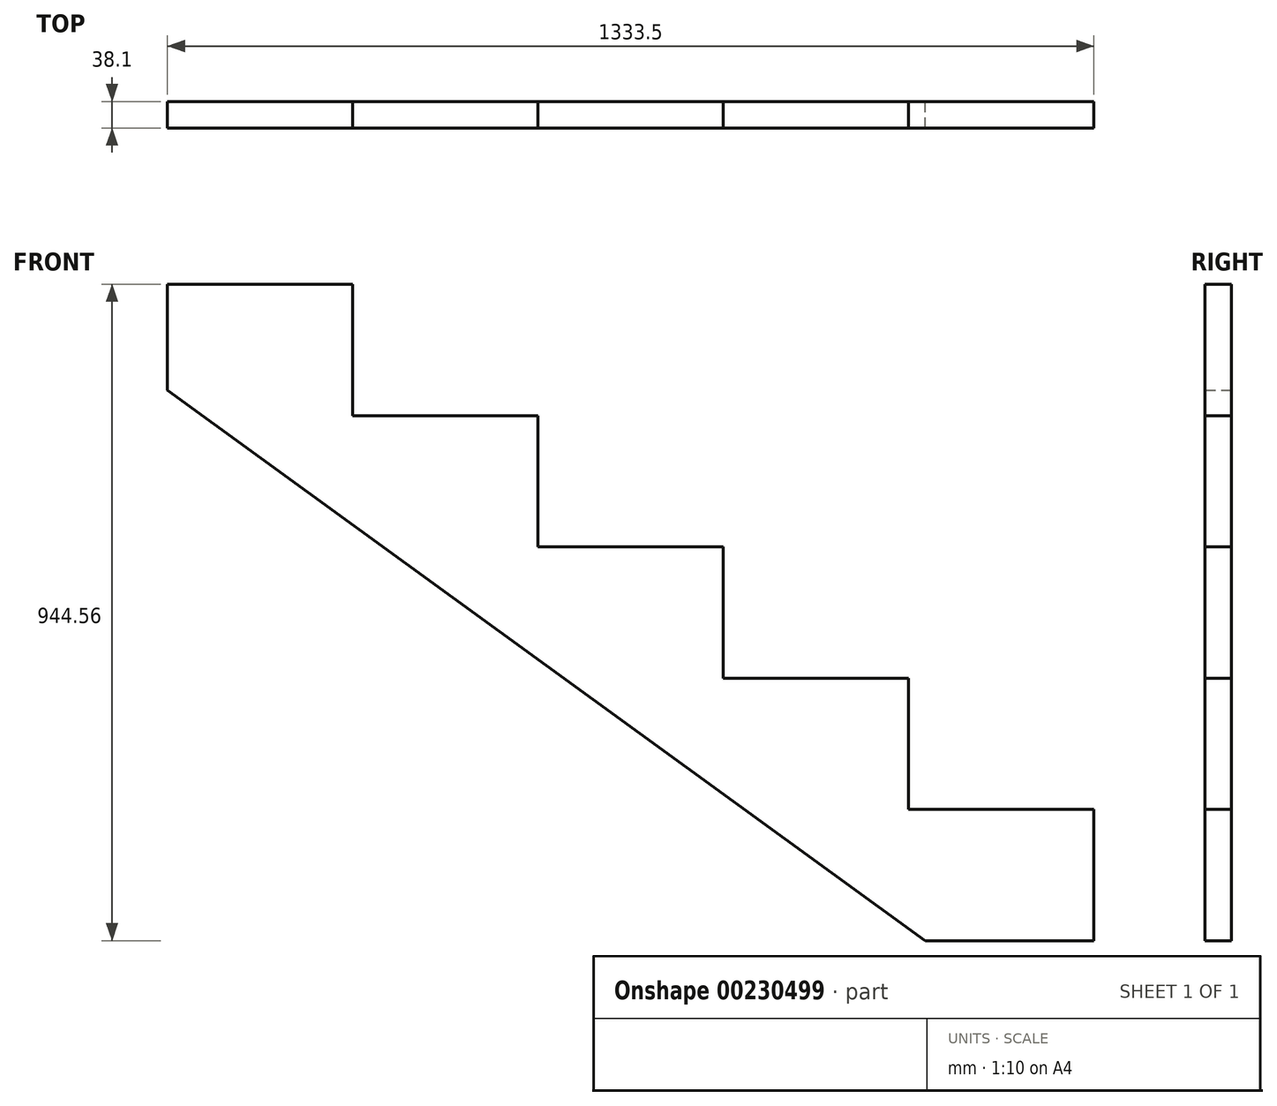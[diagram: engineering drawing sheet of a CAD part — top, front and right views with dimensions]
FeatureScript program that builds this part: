
annotation { "Feature Type Name" : "Feature", "Feature Type Description" : "" }
export const myFeature = defineFeature(function(context is Context, id is Id, definition is map)
    precondition{}
    {
        {
            var Q0;
            Q0=qCreatedBy(makeId("Front.planeOp"),FACE);
            var sketch = newSketch(context, id + "F0", { "sketchPlane" : qUnion([Q0])});
            skLineSegment(sketch, "E0", {"start": v(0, 944.56) * mm, "end": v(0, 792.16) * mm});
            skLineSegment(sketch, "E1", {"start": v(0, 792.16) * mm, "end": v(1090.32, 0) * mm});
            skLineSegment(sketch, "E2", {"start": v(1090.32, 0) * mm, "end": v(1333.5, 0) * mm});
            skLineSegment(sketch, "E3", {"start": v(0, 944.56) * mm, "end": v(266.7, 944.56) * mm});
            skLineSegment(sketch, "E4", {"start": v(1333.5, 0) * mm, "end": v(1333.5, 188.91) * mm});
            skLineSegment(sketch, "E5", {"start": v(1333.5, 188.91) * mm, "end": v(1066.8, 188.91) * mm});
            skLineSegment(sketch, "E6", {"start": v(1066.8, 188.91) * mm, "end": v(1066.8, 377.82) * mm});
            skLineSegment(sketch, "E7", {"start": v(1066.8, 377.83) * mm, "end": v(800.1, 377.83) * mm});
            skLineSegment(sketch, "E8", {"start": v(800.1, 377.83) * mm, "end": v(800.1, 566.74) * mm});
            skLineSegment(sketch, "E9", {"start": v(800.1, 566.74) * mm, "end": v(533.4, 566.74) * mm});
            skLineSegment(sketch, "E10", {"start": v(533.4, 566.74) * mm, "end": v(533.4, 755.65) * mm});
            skLineSegment(sketch, "E11", {"start": v(533.4, 755.65) * mm, "end": v(266.7, 755.65) * mm});
            skLineSegment(sketch, "E12", {"start": v(266.7, 755.65) * mm, "end": v(266.7, 944.56) * mm});
            skSolve(sketch);
        }
        {
            var Q0;
            Q0 = qSketchRegion(id + "F0", true);
            extrude(context, id + "F1", {"entities" : qUnion([Q0]), "endBound" : BoundingType.SYMMETRIC, "depth" : 38.1 * mm});
        }
    });
